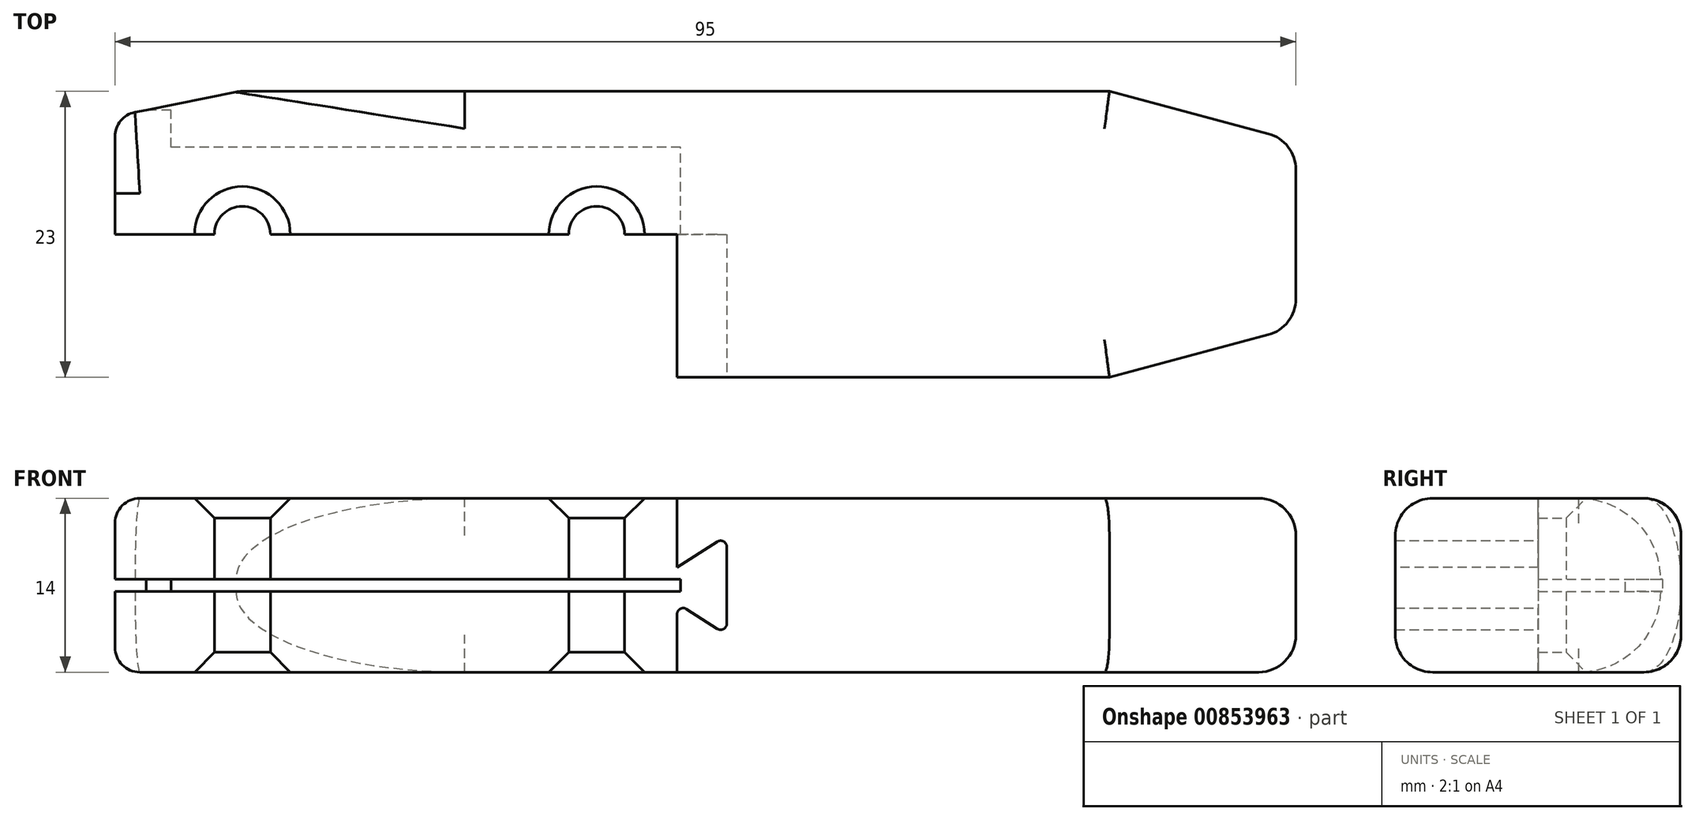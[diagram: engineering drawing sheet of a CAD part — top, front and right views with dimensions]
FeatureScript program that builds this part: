
annotation { "Feature Type Name" : "Feature", "Feature Type Description" : "" }
export const myFeature = defineFeature(function(context is Context, id is Id, definition is map)
    precondition{}
    {
        {
            var Q0;
            Q0=qCreatedBy(makeId("Top.planeOp"),FACE);
            var sketch = newSketch(context, id + "F0", { "sketchPlane" : qUnion([Q0])});
            skCircle(sketch, "E0", {"center": v(0, 0) * mm, "radius": 2.25 * mm});
            skCircle(sketch, "E1", {"center": v(-28.5, 0) * mm, "radius": 2.25 * mm});
            skPoint(sketch, "E2.start.orphan", {"position": v(86.29, 6) * mm});
            skLineSegment(sketch, "E3", {"start": v(-38.75, 11.5) * mm, "end": v(-38.75, -11.5) * mm});
            skLineSegment(sketch, "E4.bottom", {"start": v(-38.75, 11.5) * mm, "end": v(56.25, 11.5) * mm});
            skLineSegment(sketch, "E4.top", {"start": v(-38.75, -11.5) * mm, "end": v(56.25, -11.5) * mm});
            skLineSegment(sketch, "E4.right", {"start": v(56.25, 11.5) * mm, "end": v(56.25, -11.5) * mm});
            skLineSegment(sketch, "E5", {"start": v(6.25, 11.5) * mm, "end": v(6.25, -11.5) * mm, "construction": true});
            skSolve(sketch);
        }
        {
            var Q0;
            Q0=makeQuery(id+"F0.imprint","IMPRINT",FACE,{"disambiguationData":[TD([[makeQuery(id+"F0.imprint","IMPRINT",EDGE,{"derivedFrom":sQuery(id+"F0.wireOp",EDGE,"E0")}),-1.0]])]});
            extrude(context, id + "F1", {"entities" : qUnion([Q0]), "depth" : 14 * mm, "offsetDistance" : 25 * mm});
        }
        {
            var Q0;
            Q0=makeQuery(id+"F1.opExtrude","SWEPT_EDGE",EDGE,{"disambiguationData":[OSD([sQuery(id+"F0.wireOp",EDGE,"E4.bottom"),sQuery(id+"F0.wireOp",EDGE,"E3")])]});
            var Q1;
            Q1=makeQuery(id+"F1.opExtrude","SWEPT_EDGE",EDGE,{"disambiguationData":[OSD([sQuery(id+"F0.wireOp",EDGE,"E4.top"),sQuery(id+"F0.wireOp",EDGE,"E3")])]});
            chamfer(context, id + "F2", {"entities" : qUnion([Q0, Q1]), "chamferType" : ChamferType.TWO_OFFSETS, "width1" : 2 * mm, "oppositeDirection" : false, "width2" : 10 * mm, "tangentPropagation" : true});
        }
        {
            var Q0;
            {var subQ0=sQuery(id+"F0.wireOp",EDGE,"E3");var subQ1=sQuery(id+"F0.wireOp",EDGE,"E4.bottom");Q0=makeQuery(id+"F2.opChamfer","BLEND_EDGE",EDGE,{"blendedFrom":[makeQuery(id+"F1.opExtrude","SWEPT_EDGE",EDGE,{"disambiguationData":[OSD([subQ1,subQ0])]}),makeQuery(id+"F1.opExtrude","CAP_FACE",FACE,{"disambiguationData":[OSD([sQuery(id+"F0.wireOp",EDGE,"E0"),sQuery(id+"F0.wireOp",EDGE,"E1"),subQ1,sQuery(id+"F0.wireOp",EDGE,"E4.top"),subQ0,sQuery(id+"F0.wireOp",EDGE,"E4.right")])],"isStart":false})],"blendedInto":[makeQuery(id+"F1.opExtrude","CAP_FACE",FACE,{"disambiguationData":[OSD([sQuery(id+"F0.wireOp",EDGE,"E0"),sQuery(id+"F0.wireOp",EDGE,"E1"),subQ1,sQuery(id+"F0.wireOp",EDGE,"E4.top"),subQ0,sQuery(id+"F0.wireOp",EDGE,"E4.right")])],"isStart":false})]});}
            var Q1;
            {var subQ0=sQuery(id+"F0.wireOp",EDGE,"E3");var subQ1=sQuery(id+"F0.wireOp",EDGE,"E4.top");Q1=makeQuery(id+"F2.opChamfer","BLEND_EDGE",EDGE,{"blendedFrom":[makeQuery(id+"F1.opExtrude","SWEPT_EDGE",EDGE,{"disambiguationData":[OSD([subQ1,subQ0])]}),makeQuery(id+"F1.opExtrude","CAP_FACE",FACE,{"disambiguationData":[OSD([sQuery(id+"F0.wireOp",EDGE,"E0"),sQuery(id+"F0.wireOp",EDGE,"E1"),sQuery(id+"F0.wireOp",EDGE,"E4.bottom"),subQ1,subQ0,sQuery(id+"F0.wireOp",EDGE,"E4.right")])],"isStart":false})],"blendedInto":[makeQuery(id+"F1.opExtrude","CAP_FACE",FACE,{"disambiguationData":[OSD([sQuery(id+"F0.wireOp",EDGE,"E0"),sQuery(id+"F0.wireOp",EDGE,"E1"),sQuery(id+"F0.wireOp",EDGE,"E4.bottom"),subQ1,subQ0,sQuery(id+"F0.wireOp",EDGE,"E4.right")])],"isStart":false})]});}
            var Q2;
            {var subQ0=sQuery(id+"F0.wireOp",EDGE,"E3");var subQ1=sQuery(id+"F0.wireOp",EDGE,"E4.top");Q2=makeQuery(id+"F2.opChamfer","BLEND_EDGE",EDGE,{"blendedFrom":[makeQuery(id+"F1.opExtrude","SWEPT_EDGE",EDGE,{"disambiguationData":[OSD([subQ1,subQ0])]}),makeQuery(id+"F1.opExtrude","CAP_FACE",FACE,{"disambiguationData":[OSD([sQuery(id+"F0.wireOp",EDGE,"E0"),sQuery(id+"F0.wireOp",EDGE,"E1"),sQuery(id+"F0.wireOp",EDGE,"E4.bottom"),subQ1,subQ0,sQuery(id+"F0.wireOp",EDGE,"E4.right")])],"isStart":true})],"blendedInto":[makeQuery(id+"F1.opExtrude","CAP_FACE",FACE,{"disambiguationData":[OSD([sQuery(id+"F0.wireOp",EDGE,"E0"),sQuery(id+"F0.wireOp",EDGE,"E1"),sQuery(id+"F0.wireOp",EDGE,"E4.bottom"),subQ1,subQ0,sQuery(id+"F0.wireOp",EDGE,"E4.right")])],"isStart":true})]});}
            var Q3;
            {var subQ0=sQuery(id+"F0.wireOp",EDGE,"E3");var subQ1=sQuery(id+"F0.wireOp",EDGE,"E4.bottom");Q3=makeQuery(id+"F2.opChamfer","BLEND_EDGE",EDGE,{"blendedFrom":[makeQuery(id+"F1.opExtrude","SWEPT_EDGE",EDGE,{"disambiguationData":[OSD([subQ1,subQ0])]}),makeQuery(id+"F1.opExtrude","CAP_FACE",FACE,{"disambiguationData":[OSD([sQuery(id+"F0.wireOp",EDGE,"E0"),sQuery(id+"F0.wireOp",EDGE,"E1"),subQ1,sQuery(id+"F0.wireOp",EDGE,"E4.top"),subQ0,sQuery(id+"F0.wireOp",EDGE,"E4.right")])],"isStart":true})],"blendedInto":[makeQuery(id+"F1.opExtrude","CAP_FACE",FACE,{"disambiguationData":[OSD([sQuery(id+"F0.wireOp",EDGE,"E0"),sQuery(id+"F0.wireOp",EDGE,"E1"),subQ1,sQuery(id+"F0.wireOp",EDGE,"E4.top"),subQ0,sQuery(id+"F0.wireOp",EDGE,"E4.right")])],"isStart":true})]});}
            fillet(context, id + "F3", {"entities" : qUnion([Q0, Q1, Q2, Q3]), "radius" : 6.5 * mm, "allowEdgeOverflow" : false});
        }
        {
            var Q0;
            Q0=makeQuery(id+"F1.opExtrude","SWEPT_EDGE",EDGE,{"disambiguationData":[OSD([sQuery(id+"F0.wireOp",EDGE,"E4.bottom"),sQuery(id+"F0.wireOp",EDGE,"E4.right")])]});
            var Q1;
            Q1=makeQuery(id+"F1.opExtrude","SWEPT_EDGE",EDGE,{"disambiguationData":[OSD([sQuery(id+"F0.wireOp",EDGE,"E4.top"),sQuery(id+"F0.wireOp",EDGE,"E4.right")])]});
            chamfer(context, id + "F4", {"entities" : qUnion([Q0, Q1]), "chamferType" : ChamferType.TWO_OFFSETS, "width1" : 4 * mm, "oppositeDirection" : true, "width2" : 15 * mm});
        }
        {
            var Q0;
            Q0=makeQuery(id+"F1.opExtrude","CAP_EDGE",EDGE,{"disambiguationData":[OSD([sQuery(id+"F0.wireOp",EDGE,"E4.top")])],"isStart":true});
            var Q1;
            Q1=makeQuery(id+"F1.opExtrude","CAP_EDGE",EDGE,{"disambiguationData":[OSD([sQuery(id+"F0.wireOp",EDGE,"E4.bottom")])],"isStart":true});
            var Q2;
            {var subQ0=sQuery(id+"F0.wireOp",EDGE,"E4.right");var subQ1=sQuery(id+"F0.wireOp",EDGE,"E4.top");Q2=makeQuery(id+"F4.opChamfer","BLEND_EDGE",EDGE,{"blendedFrom":[makeQuery(id+"F1.opExtrude","SWEPT_EDGE",EDGE,{"disambiguationData":[OSD([subQ1,subQ0])]}),makeQuery(id+"F1.opExtrude","CAP_FACE",FACE,{"disambiguationData":[OSD([sQuery(id+"F0.wireOp",EDGE,"E0"),sQuery(id+"F0.wireOp",EDGE,"E1"),sQuery(id+"F0.wireOp",EDGE,"E4.bottom"),subQ1,sQuery(id+"F0.wireOp",EDGE,"E3"),subQ0])],"isStart":false})],"blendedInto":[makeQuery(id+"F1.opExtrude","CAP_FACE",FACE,{"disambiguationData":[OSD([sQuery(id+"F0.wireOp",EDGE,"E0"),sQuery(id+"F0.wireOp",EDGE,"E1"),sQuery(id+"F0.wireOp",EDGE,"E4.bottom"),subQ1,sQuery(id+"F0.wireOp",EDGE,"E3"),subQ0])],"isStart":false})]});}
            var Q3;
            {var subQ0=sQuery(id+"F0.wireOp",EDGE,"E4.right");var subQ1=sQuery(id+"F0.wireOp",EDGE,"E4.bottom");Q3=makeQuery(id+"F4.opChamfer","BLEND_EDGE",EDGE,{"blendedFrom":[makeQuery(id+"F1.opExtrude","SWEPT_EDGE",EDGE,{"disambiguationData":[OSD([subQ1,subQ0])]}),makeQuery(id+"F1.opExtrude","CAP_FACE",FACE,{"disambiguationData":[OSD([sQuery(id+"F0.wireOp",EDGE,"E0"),sQuery(id+"F0.wireOp",EDGE,"E1"),subQ1,sQuery(id+"F0.wireOp",EDGE,"E4.top"),sQuery(id+"F0.wireOp",EDGE,"E3"),subQ0])],"isStart":false})],"blendedInto":[makeQuery(id+"F1.opExtrude","CAP_FACE",FACE,{"disambiguationData":[OSD([sQuery(id+"F0.wireOp",EDGE,"E0"),sQuery(id+"F0.wireOp",EDGE,"E1"),subQ1,sQuery(id+"F0.wireOp",EDGE,"E4.top"),sQuery(id+"F0.wireOp",EDGE,"E3"),subQ0])],"isStart":false})]});}
            var Q4;
            {var subQ0=sQuery(id+"F0.wireOp",EDGE,"E4.right");var subQ1=sQuery(id+"F0.wireOp",EDGE,"E4.bottom");Q4=makeQuery(id+"F4.opChamfer","BLEND_EDGE",EDGE,{"blendedFrom":[makeQuery(id+"F1.opExtrude","SWEPT_EDGE",EDGE,{"disambiguationData":[OSD([subQ1,subQ0])]}),makeQuery(id+"F1.opExtrude","CAP_FACE",FACE,{"disambiguationData":[OSD([sQuery(id+"F0.wireOp",EDGE,"E0"),sQuery(id+"F0.wireOp",EDGE,"E1"),subQ1,sQuery(id+"F0.wireOp",EDGE,"E4.top"),sQuery(id+"F0.wireOp",EDGE,"E3"),subQ0])],"isStart":true})],"blendedInto":[makeQuery(id+"F1.opExtrude","CAP_FACE",FACE,{"disambiguationData":[OSD([sQuery(id+"F0.wireOp",EDGE,"E0"),sQuery(id+"F0.wireOp",EDGE,"E1"),subQ1,sQuery(id+"F0.wireOp",EDGE,"E4.top"),sQuery(id+"F0.wireOp",EDGE,"E3"),subQ0])],"isStart":true})]});}
            var Q5;
            {var subQ0=sQuery(id+"F0.wireOp",EDGE,"E4.right");var subQ1=sQuery(id+"F0.wireOp",EDGE,"E4.top");Q5=makeQuery(id+"F4.opChamfer","BLEND_EDGE",EDGE,{"blendedFrom":[makeQuery(id+"F1.opExtrude","SWEPT_EDGE",EDGE,{"disambiguationData":[OSD([subQ1,subQ0])]}),makeQuery(id+"F1.opExtrude","CAP_FACE",FACE,{"disambiguationData":[OSD([sQuery(id+"F0.wireOp",EDGE,"E0"),sQuery(id+"F0.wireOp",EDGE,"E1"),sQuery(id+"F0.wireOp",EDGE,"E4.bottom"),subQ1,sQuery(id+"F0.wireOp",EDGE,"E3"),subQ0])],"isStart":true})],"blendedInto":[makeQuery(id+"F1.opExtrude","CAP_FACE",FACE,{"disambiguationData":[OSD([sQuery(id+"F0.wireOp",EDGE,"E0"),sQuery(id+"F0.wireOp",EDGE,"E1"),sQuery(id+"F0.wireOp",EDGE,"E4.bottom"),subQ1,sQuery(id+"F0.wireOp",EDGE,"E3"),subQ0])],"isStart":true})]});}
            var Q6;
            Q6=makeQuery(id+"F1.opExtrude","SWEPT_FACE",FACE,{"disambiguationData":[OSD([sQuery(id+"F0.wireOp",EDGE,"E4.right")])]});
            fillet(context, id + "F5", {"entities" : qUnion([Q0, Q1, Q2, Q3, Q4, Q5, Q6]), "radius" : 3 * mm, "tangentPropagation" : true, "allowEdgeOverflow" : false});
        }
        {
            var Q0;
            Q0=makeQuery(id+"F1.opExtrude","SWEPT_FACE",FACE,{"disambiguationData":[OSD([sQuery(id+"F0.wireOp",EDGE,"E3")])]});
            fillet(context, id + "F6", {"entities" : qUnion([Q0]), "radius" : 2 * mm, "tangentPropagation" : true, "allowEdgeOverflow" : false});
        }
        {
            var Q0;
            Q0=makeQuery(id+"F1.opExtrude","CAP_FACE",FACE,{"disambiguationData":[OSD([sQuery(id+"F0.wireOp",EDGE,"E0"),sQuery(id+"F0.wireOp",EDGE,"E1"),sQuery(id+"F0.wireOp",EDGE,"E4.bottom"),sQuery(id+"F0.wireOp",EDGE,"E4.top"),sQuery(id+"F0.wireOp",EDGE,"E3"),sQuery(id+"F0.wireOp",EDGE,"E4.right")])],"isStart":false});
            var sketch = newSketch(context, id + "F7", { "sketchPlane" : qUnion([Q0])});
            skLineSegment(sketch, "E6.bottom", {"start": v(-41.82, -15.17) * mm, "end": v(6.47, -15.17) * mm});
            skLineSegment(sketch, "E6.top", {"start": v(-41.82, 0) * mm, "end": v(6.47, 0) * mm});
            skLineSegment(sketch, "E6.left", {"start": v(-41.82, -15.17) * mm, "end": v(-41.82, 0) * mm});
            skLineSegment(sketch, "E6.right", {"start": v(6.47, -15.17) * mm, "end": v(6.47, 0) * mm});
            skSolve(sketch);
        }
        {
            var Q0;
            Q0 = qSketchRegion(id + "F7", true);
            extrude(context, id + "F8", {"entities" : qUnion([Q0]), "operationType" : NewBodyOperationType.REMOVE, "oppositeDirection" : true, "depth" : 25 * mm, "offsetDistance" : 25 * mm});
        }
        {
            var Q0;
            Q0=makeQuery(id+"F1.opExtrude","SWEPT_FACE",FACE,{"disambiguationData":[OSD([sQuery(id+"F0.wireOp",EDGE,"E4.top")])]});
            var sketch = newSketch(context, id + "F9", { "sketchPlane" : qUnion([Q0])});
            skLineSegment(sketch, "E7", {"start": v(6.47, 8.42) * mm, "end": v(10.47, 11) * mm});
            skLineSegment(sketch, "E8", {"start": v(10.47, 11) * mm, "end": v(10.47, 3) * mm});
            skLineSegment(sketch, "E9", {"start": v(10.47, 3) * mm, "end": v(6.47, 5.58) * mm});
            skLineSegment(sketch, "E10", {"start": v(6.47, 8.42) * mm, "end": v(6.47, 5.58) * mm});
            skSolve(sketch);
        }
        {
            var Q0;
            Q0=makeQuery(id+"F9.imprint","IMPRINT",FACE,{"disambiguationData":[TD([[makeQuery(id+"F9.imprint","IMPRINT",EDGE,{"derivedFrom":sQuery(id+"F9.wireOp",EDGE,"E7")}),-1.0]])]});
            extrude(context, id + "F10", {"entities" : qUnion([Q0]), "operationType" : NewBodyOperationType.REMOVE, "oppositeDirection" : true, "depth" : 11.5 * mm, "offsetDistance" : 25 * mm});
        }
        {
            var Q0;
            Q0=makeQuery(id+"F10.boolean.opBoolean","COPY",EDGE,{"derivedFrom":makeQuery(id+"F10.opExtrude","SWEPT_EDGE",EDGE,{"disambiguationData":[OSD([sQuery(id+"F0.wireOp",EDGE,"E4.top"),sQuery(id+"F9.wireOp",EDGE,"E7"),sQuery(id+"F9.wireOp",EDGE,"E8")])]})});
            var Q1;
            Q1=makeQuery(id+"F10.boolean.opBoolean","COPY",EDGE,{"derivedFrom":makeQuery(id+"F10.opExtrude","SWEPT_EDGE",EDGE,{"disambiguationData":[OSD([sQuery(id+"F0.wireOp",EDGE,"E4.top"),sQuery(id+"F7.wireOp",EDGE,"E6.right"),sQuery(id+"F9.wireOp",EDGE,"E7"),sQuery(id+"F9.wireOp",EDGE,"E10")])]})});
            var Q2;
            Q2=makeQuery(id+"F10.boolean.opBoolean","COPY",EDGE,{"derivedFrom":makeQuery(id+"F10.opExtrude","SWEPT_EDGE",EDGE,{"disambiguationData":[OSD([sQuery(id+"F0.wireOp",EDGE,"E4.top"),sQuery(id+"F9.wireOp",EDGE,"E8"),sQuery(id+"F9.wireOp",EDGE,"E9")])]})});
            var Q3;
            Q3=makeQuery(id+"F10.boolean.opBoolean","COPY",EDGE,{"derivedFrom":makeQuery(id+"F10.opExtrude","SWEPT_EDGE",EDGE,{"disambiguationData":[OSD([sQuery(id+"F0.wireOp",EDGE,"E4.top"),sQuery(id+"F7.wireOp",EDGE,"E6.right"),sQuery(id+"F9.wireOp",EDGE,"E9"),sQuery(id+"F9.wireOp",EDGE,"E10")])]})});
            fillet(context, id + "F11", {"entities" : qUnion([Q0, Q1, Q2, Q3]), "radius" : .5 * mm, "tangentPropagation" : true, "allowEdgeOverflow" : false});
        }
        {
            var Q0;
            Q0=makeQuery(id+"F1.opExtrude","SWEPT_FACE",FACE,{"disambiguationData":[OSD([sQuery(id+"F0.wireOp",EDGE,"E3")])]});
            var sketch = newSketch(context, id + "F12", { "sketchPlane" : qUnion([Q0])});
            skLineSegment(sketch, "E11.bottom", {"start": v(10, 7.5) * mm, "end": v(-10, 7.5) * mm});
            skLineSegment(sketch, "E11.top", {"start": v(10, 6.5) * mm, "end": v(-10, 6.5) * mm});
            skLineSegment(sketch, "E11.left", {"start": v(10, 7.5) * mm, "end": v(10, 6.5) * mm});
            skLineSegment(sketch, "E11.right", {"start": v(-10, 7.5) * mm, "end": v(-10, 6.5) * mm});
            skSolve(sketch);
        }
        {
            var Q0;
            {var subQ0=sQuery(id+"F12.wireOp",EDGE,"E11.left");Q0=makeQuery(id+"F12.imprint","IMPRINT",FACE,{"disambiguationData":[TD([[makeQuery(id+"F12.imprint","IMPRINT",EDGE,{"derivedFrom":subQ0}),-1.0]])]});}
            var Q1;
            {var subQ1=sQuery(id+"F0.wireOp",EDGE,"E3");var subQ2=makeQuery(id+"F1.opExtrude","SWEPT_FACE",FACE,{"disambiguationData":[OSD([subQ1])]});var subQ3=subQ2;var subQ4=subQ3;var subQ5=sQuery(id+"F0.wireOp",EDGE,"E4.bottom");var subQ6=makeQuery(id+"F1.opExtrude","SWEPT_EDGE",EDGE,{"disambiguationData":[OSD([subQ5,subQ1])]});var subQ7=makeQuery(id+"F6.opFillet","BLEND_EDGE",EDGE,{"blendedFrom":[makeQuery(id+"F2.opChamfer","BLEND_EDGE",EDGE,{"blendedFrom":[subQ6,subQ2],"blendedInto":[subQ2]}),subQ4],"blendedInto":[subQ4]});Q1=makeQuery(id+"F12.imprint","IMPRINT",FACE,{"disambiguationData":[TD([[makeQuery(id+"F12.imprint","IMPRINT",EDGE,{"derivedFrom":subQ7}),1.0]])]});}
            var Q2;
            {var subQ12=sQuery(id+"F12.wireOp",EDGE,"E11.right");Q2=makeQuery(id+"F12.imprint","IMPRINT",FACE,{"disambiguationData":[TD([[makeQuery(id+"F12.imprint","IMPRINT",EDGE,{"derivedFrom":subQ12}),1.0]])]});}
            extrude(context, id + "F13", {"entities" : qUnion([Q0, Q1, Q2]), "operationType" : NewBodyOperationType.REMOVE, "oppositeDirection" : true, "depth" : 4.5 * mm, "offsetDistance" : 25 * mm});
        }
        {
            var Q0;
            Q0=makeQuery(id+"F13.boolean.opBoolean","COPY",FACE,{"derivedFrom":makeQuery(id+"F13.opExtrude","CAP_FACE",FACE,{"disambiguationData":[OSD([sQuery(id+"F12.wireOp",EDGE,"E11.bottom"),sQuery(id+"F12.wireOp",EDGE,"E11.top"),sQuery(id+"F12.wireOp",EDGE,"E11.left"),sQuery(id+"F12.wireOp",EDGE,"E11.right")])],"isStart":false})});
            var sketch = newSketch(context, id + "F14", { "sketchPlane" : qUnion([Q0])});
            skLineSegment(sketch, "E12.bottom", {"start": v(0, 6.5) * mm, "end": v(-7, 6.5) * mm});
            skLineSegment(sketch, "E12.top", {"start": v(0, 7.5) * mm, "end": v(-7, 7.5) * mm});
            skLineSegment(sketch, "E12.left", {"start": v(0, 6.5) * mm, "end": v(0, 7.5) * mm});
            skLineSegment(sketch, "E12.right", {"start": v(-7, 6.5) * mm, "end": v(-7, 7.5) * mm});
            skSolve(sketch);
        }
        {
            var Q0;
            Q0 = qSketchRegion(id + "F14", true);
            extrude(context, id + "F15", {"entities" : qUnion([Q0]), "operationType" : NewBodyOperationType.REMOVE, "oppositeDirection" : true, "depth" : 41 * mm, "offsetDistance" : 25 * mm});
        }
        {
            var Q0;
            Q0=makeQuery(id+"F1.opExtrude","CAP_EDGE",EDGE,{"disambiguationData":[OSD([sQuery(id+"F0.wireOp",EDGE,"E1")])],"isStart":false});
            var Q1;
            Q1=makeQuery(id+"F1.opExtrude","CAP_EDGE",EDGE,{"disambiguationData":[OSD([sQuery(id+"F0.wireOp",EDGE,"E0")])],"isStart":false});
            var Q2;
            Q2=makeQuery(id+"F1.opExtrude","CAP_EDGE",EDGE,{"disambiguationData":[OSD([sQuery(id+"F0.wireOp",EDGE,"E1")])],"isStart":true});
            var Q3;
            Q3=makeQuery(id+"F1.opExtrude","CAP_EDGE",EDGE,{"disambiguationData":[OSD([sQuery(id+"F0.wireOp",EDGE,"E0")])],"isStart":true});
            chamfer(context, id + "F16", {"entities" : qUnion([Q0, Q1, Q2, Q3]), "width" : 1.6 * mm, "tangentPropagation" : true});
        }
    });
